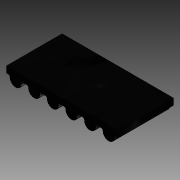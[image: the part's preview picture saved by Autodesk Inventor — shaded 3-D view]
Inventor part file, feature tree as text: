
AUTODESK INVENTOR PART (.ipt)
format: ipt  version: 2014 (Build 180170000, 170)  size: 112,128 bytes
history: native  units: mm
features: extrude x1, sketch x1
ambient origin geometry x8: Origin, YZ Plane, XZ Plane, XY Plane, X Axis, Y Axis, Z Axis, Center Point
bodies: Solid1 (feature_tree)
feature tree (2):
  extrude  "Extrusion1"  [1 undecoded]
  sketch  "Sketch1"  dims[d0=15.0mm d1=0.0mm]
note: 1 required parameter value undecoded (feature->parameter linkage not recoverable at this tier; creation-order binding heuristic only, values carry confidence <= 0.55)
